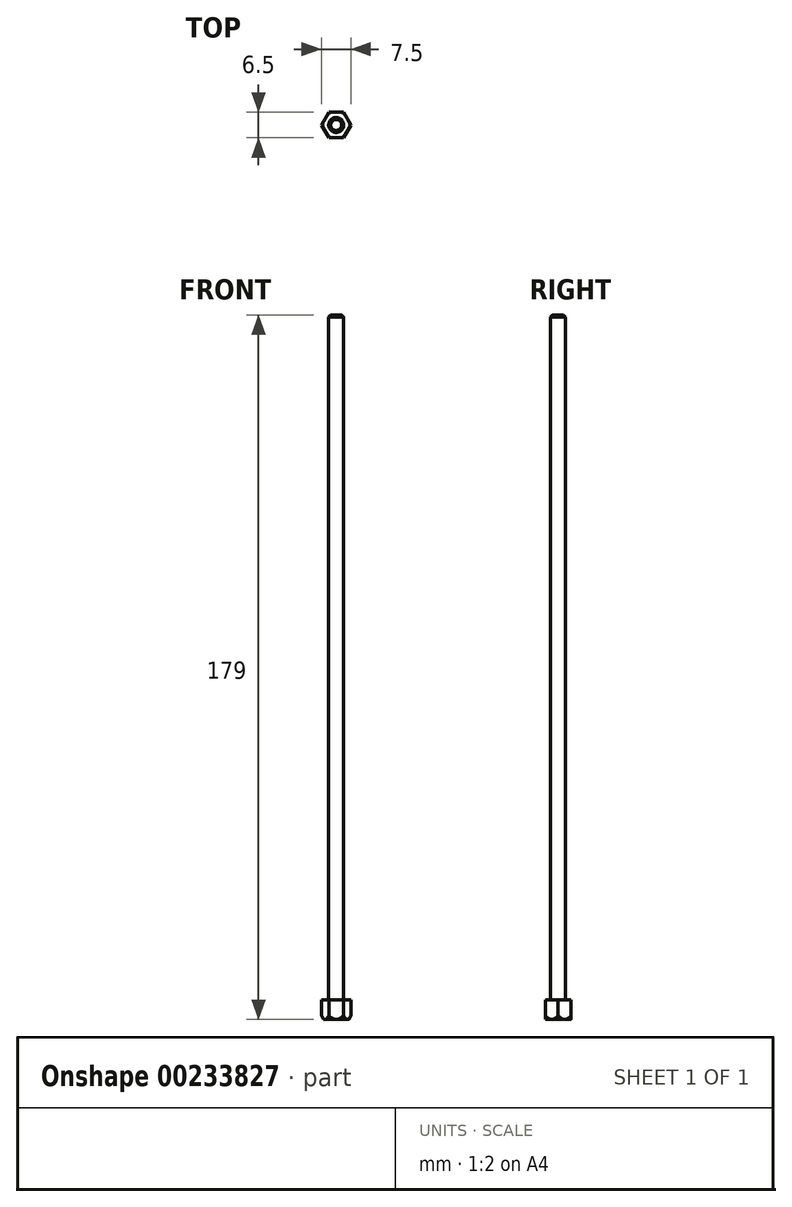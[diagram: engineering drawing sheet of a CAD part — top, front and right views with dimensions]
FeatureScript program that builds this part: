
annotation { "Feature Type Name" : "Feature", "Feature Type Description" : "" }
export const myFeature = defineFeature(function(context is Context, id is Id, definition is map)
    precondition{}
    {
        {
            var Q0;
            Q0=qCreatedBy(makeId("Top.planeOp"),FACE);
            var sketch = newSketch(context, id + "F0", { "sketchPlane" : qUnion([Q0])});
            skCircle(sketch, "E0.cCircle", {"center": v(0, 0) * mm, "radius": 3.25 * mm, "construction": true});
            skLineSegment(sketch, "E0.0", {"start": v(1.88, 3.25) * mm, "end": v(3.75, 0) * mm});
            skLineSegment(sketch, "E0.1", {"start": v(3.75, 0) * mm, "end": v(1.88, -3.25) * mm});
            skLineSegment(sketch, "E0.2", {"start": v(1.87, -3.25) * mm, "end": v(-1.88, -3.25) * mm});
            skLineSegment(sketch, "E0.3", {"start": v(-1.88, -3.25) * mm, "end": v(-3.75, 0) * mm});
            skLineSegment(sketch, "E0.4", {"start": v(-3.75, 0) * mm, "end": v(-1.88, 3.25) * mm});
            skLineSegment(sketch, "E0.5", {"start": v(-1.87, 3.25) * mm, "end": v(1.88, 3.25) * mm});
            skPoint(sketch, "E0.0.midPoint", {"position": v(2.81, 1.62) * mm});
            skCircle(sketch, "E1", {"center": v(0, 0) * mm, "radius": 1.9 * mm});
            skCircle(sketch, "E2", {"center": v(0, 0) * mm, "radius": 2.5 * mm});
            skSolve(sketch);
        }
        {
            var Q0;
            Q0=makeQuery(id+"F0.imprint","IMPRINT",FACE,{"disambiguationData":[TD([[makeQuery(id+"F0.imprint","IMPRINT",EDGE,{"derivedFrom":sQuery(id+"F0.wireOp",EDGE,"E0.0")}),-1.0]])]});
            var Q1;
            Q1=makeQuery(id+"F0.imprint","IMPRINT",FACE,{"disambiguationData":[TD([[makeQuery(id+"F0.imprint","IMPRINT",EDGE,{"derivedFrom":sQuery(id+"F0.wireOp",EDGE,"E1")}),-1.0]])]});
            extrude(context, id + "F1", {"entities" : qUnion([Q0, Q1]), "depth" : 5 * mm});
        }
        {
            var Q0;
            Q0=makeQuery(id+"F0.imprint","IMPRINT",FACE,{"disambiguationData":[TD([[makeQuery(id+"F0.imprint","IMPRINT",EDGE,{"derivedFrom":sQuery(id+"F0.wireOp",EDGE,"E1")}),1.0]])]});
            extrude(context, id + "F2", {"entities" : qUnion([Q0]), "operationType" : NewBodyOperationType.ADD, "depth" : (174 + 5) * mm});
        }
        {
            var Q0;
            Q0=makeQuery(id+"F0.imprint","IMPRINT",FACE,{"disambiguationData":[TD([[makeQuery(id+"F0.imprint","IMPRINT",EDGE,{"derivedFrom":sQuery(id+"F0.wireOp",EDGE,"E0.0")}),-1.0]])]});
            var sketch = newSketch(context, id + "F3", { "sketchPlane" : qUnion([Q0])});
            skCircle(sketch, "E3", {"center": v(0, 0) * mm, "radius": 3.25 * mm});
            skSolve(sketch);
        }
        {
            var Q0;
            Q0=makeQuery(id+"F1.opExtrude","SWEPT_FACE",FACE,{"disambiguationData":[OSD([sQuery(id+"F0.wireOp",EDGE,"E0.5")])]});
            var sketch = newSketch(context, id + "F4", { "sketchPlane" : qUnion([Q0])});
            skLineSegment(sketch, "E4.0", {"start": v(-3.25, 0) * mm, "end": v(3.25, 0) * mm});
            skLineSegment(sketch, "E5", {"start": v(-3.75, 1) * mm, "end": v(-3.75, 0) * mm});
            skLineSegment(sketch, "E6", {"start": v(-3.75, 0) * mm, "end": v(-3.25, 0) * mm});
            skLineSegment(sketch, "E7", {"start": v(-3.25, 0) * mm, "end": v(-3.75, 1) * mm});
            skLineSegment(sketch, "E8", {"start": v(0, -1.89) * mm, "end": v(0, 5.76) * mm});
            skPoint(sketch, "E8.endSnap0", {"position": v(0, 5) * mm});
            skSolve(sketch);
        }
        {
            var Q0;
            Q0=qCreatedBy(makeId("Front.planeOp"),FACE);
            var sketch = newSketch(context, id + "F5", { "sketchPlane" : qUnion([Q0])});
            skPoint(sketch, "E9.0", {"position": v(3.5, 0) * mm});
            skLineSegment(sketch, "E10.0", {"start": v(3.25, 0) * mm, "end": v(3.75, 1) * mm});
            skLineSegment(sketch, "E11.0", {"start": v(3.75, 0) * mm, "end": v(3.25, 0) * mm});
            skLineSegment(sketch, "E11.1", {"start": v(3.75, 1) * mm, "end": v(3.75, 0) * mm});
            skLineSegment(sketch, "E11.2", {"start": v(3.25, 0) * mm, "end": v(-3.25, 0) * mm});
            skLineSegment(sketch, "E11.4", {"start": v(1.88, 5) * mm, "end": v(3.75, 5) * mm});
            skPoint(sketch, "E12.0", {"position": v(3.25, 0) * mm});
            skLineSegment(sketch, "E13.0", {"start": v(0, -1.89) * mm, "end": v(0, 5.76) * mm});
            skSolve(sketch);
        }
        {
            var Q0;
            Q0 = qSketchRegion(id + "F5", true);
            var Q1;
            Q1=sQuery(id+"F5.wireOp",EDGE,"E13.0");
            revolve(context, id + "F6", {"operationType" : NewBodyOperationType.REMOVE, "entities" : qUnion([Q0]), "axis" : qUnion([Q1]), "revolveType" : RevolveType.FULL, "oppositeDirection" : true});
        }
        {
            var Q0;
            Q0=makeQuery(id+"F2.opExtrude","CAP_EDGE",EDGE,{"disambiguationData":[OSD([sQuery(id+"F0.wireOp",EDGE,"E1")])],"isStart":false});
            chamfer(context, id + "F7", {"entities" : qUnion([Q0]), "width" : .5 * mm, "tangentPropagation" : true});
        }
    });
